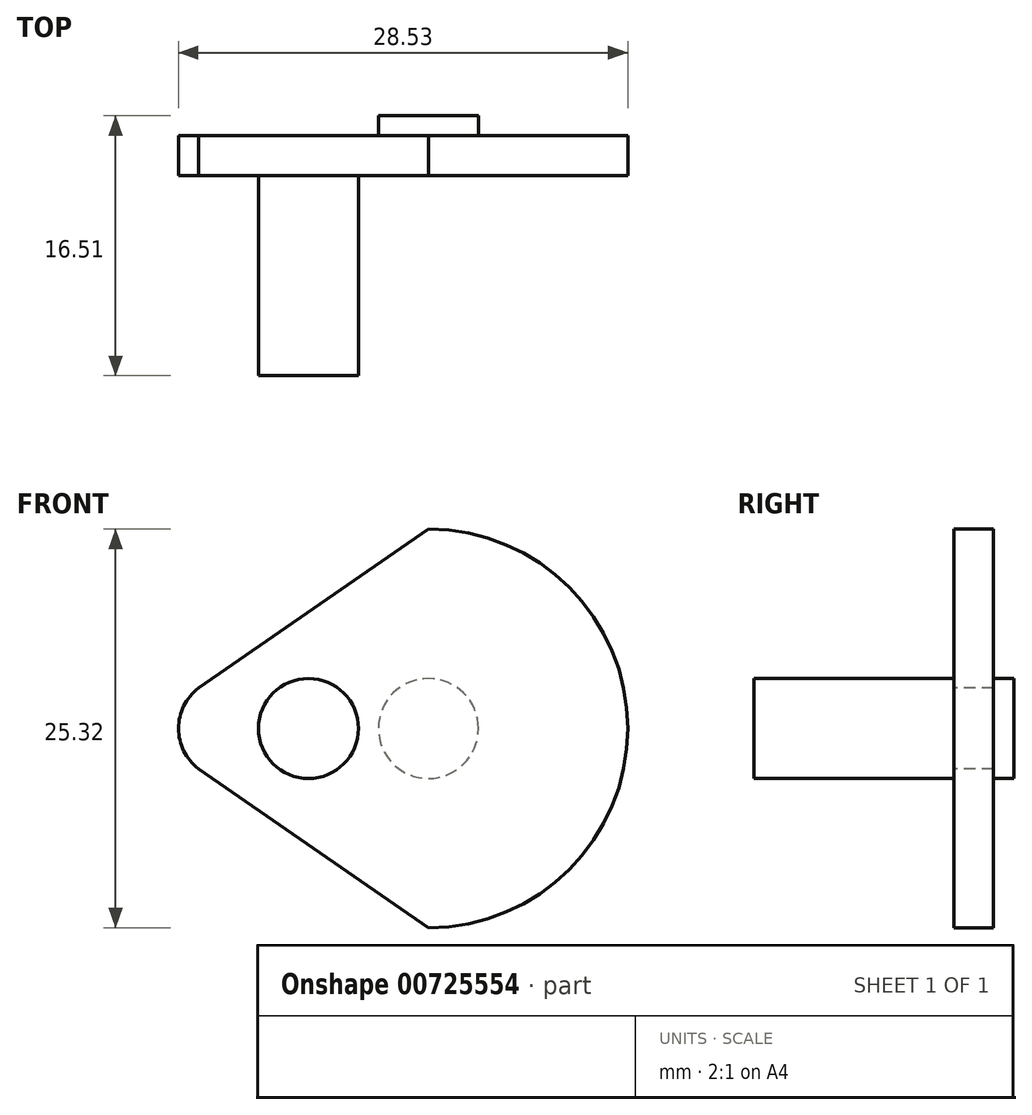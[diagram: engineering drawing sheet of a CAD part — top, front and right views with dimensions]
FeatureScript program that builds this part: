
annotation { "Feature Type Name" : "Feature", "Feature Type Description" : "" }
export const myFeature = defineFeature(function(context is Context, id is Id, definition is map)
    precondition{}
    {
        {
            var Q0;
            Q0=qCreatedBy(makeId("Front.planeOp"),FACE);
            var sketch = newSketch(context, id + "F0", { "sketchPlane" : qUnion([Q0])});
            skCircle(sketch, "E0", {"center": v(0, 0) * mm, "radius": 12.7 * mm});
            skSolve(sketch);
        }
        {
            var Q0;
            Q0=qCreatedBy(makeId("Front.planeOp"),FACE);
            var sketch = newSketch(context, id + "F1", { "sketchPlane" : qUnion([Q0])});
            skCircle(sketch, "E1", {"center": v(-7.62, 0) * mm, "radius": 3.18 * mm});
            skSolve(sketch);
        }
        {
            var Q0;
            Q0=makeQuery(id+"F1.imprint","IMPRINT",FACE,{"disambiguationData":[TD([[makeQuery(id+"F1.imprint","IMPRINT",EDGE,{"derivedFrom":sQuery(id+"F1.wireOp",EDGE,"E1")}),1.0]])]});
            extrude(context, id + "F2", {"entities" : qUnion([Q0]), "depth" : 12.7 * mm, "offsetDistance" : 25.4 * mm});
        }
        {
            var Q0;
            Q0=qCreatedBy(makeId("Front.planeOp"),FACE);
            var sketch = newSketch(context, id + "F3", { "sketchPlane" : qUnion([Q0])});
            skArc(sketch, "E2", {"start": v(0, -12.66) * mm, "mid": v(12.66, 0) * mm, "end": v(0, 12.66) * mm});
            skLineSegment(sketch, "E3", {"start": v(0, 12.66) * mm, "end": v(-14.6, 2.56) * mm});
            skArc(sketch, "E4", {"start": v(-14.6, 2.56) * mm, "mid": v(-15.87, 0) * mm, "end": v(-14.6, -2.56) * mm});
            skLineSegment(sketch, "E5", {"start": v(-14.6, -2.56) * mm, "end": v(0, -12.66) * mm});
            skSolve(sketch);
        }
        {
            var Q0;
            Q0=makeQuery(id+"F3.imprint","IMPRINT",FACE,{"disambiguationData":[TD([[makeQuery(id+"F3.imprint","IMPRINT",EDGE,{"derivedFrom":sQuery(id+"F3.wireOp",EDGE,"E2")}),1.0]])]});
            extrude(context, id + "F4", {"entities" : qUnion([Q0]), "operationType" : NewBodyOperationType.ADD, "oppositeDirection" : true, "depth" : 2.54 * mm, "offsetDistance" : 25.4 * mm});
        }
        {
            var Q0;
            Q0=makeQuery(id+"F4.opExtrude","CAP_FACE",FACE,{"disambiguationData":[OSD([sQuery(id+"F3.wireOp",EDGE,"E2"),sQuery(id+"F3.wireOp",EDGE,"E3"),sQuery(id+"F3.wireOp",EDGE,"E4"),sQuery(id+"F3.wireOp",EDGE,"E5")])],"isStart":false});
            var sketch = newSketch(context, id + "F5", { "sketchPlane" : qUnion([Q0])});
            skCircle(sketch, "E6", {"center": v(0, 0) * mm, "radius": 3.18 * mm});
            skSolve(sketch);
        }
        {
            var Q0;
            Q0=makeQuery(id+"F5.imprint","IMPRINT",FACE,{"disambiguationData":[TD([[makeQuery(id+"F5.imprint","IMPRINT",EDGE,{"derivedFrom":sQuery(id+"F5.wireOp",EDGE,"E6")}),1.0]])]});
            extrude(context, id + "F6", {"entities" : qUnion([Q0]), "operationType" : NewBodyOperationType.ADD, "depth" : 1.27 * mm, "offsetDistance" : 25.4 * mm});
        }
    });
